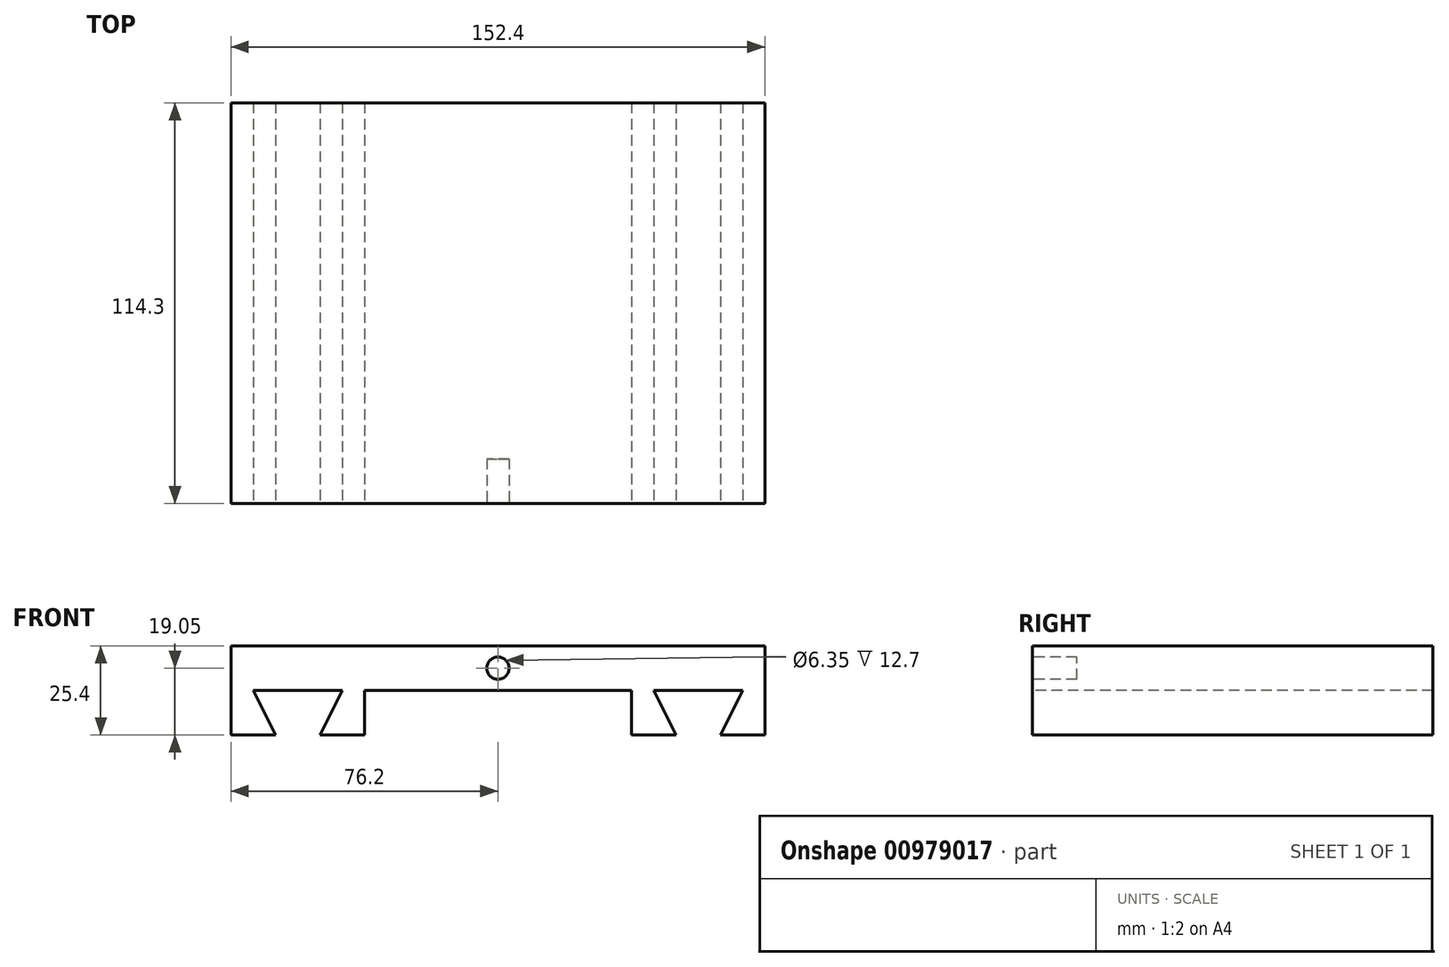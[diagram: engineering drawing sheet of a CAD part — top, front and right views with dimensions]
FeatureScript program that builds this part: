
annotation { "Feature Type Name" : "Feature", "Feature Type Description" : "" }
export const myFeature = defineFeature(function(context is Context, id is Id, definition is map)
    precondition{}
    {
        {
            var Q0;
            Q0=qCreatedBy(makeId("Top.planeOp"),FACE);
            var sketch = newSketch(context, id + "F0", { "sketchPlane" : qUnion([Q0])});
            skLineSegment(sketch, "E0.bottom", {"start": v(-76.2, 57.15) * mm, "end": v(76.2, 57.15) * mm});
            skLineSegment(sketch, "E0.top", {"start": v(-76.2, -57.15) * mm, "end": v(76.2, -57.15) * mm});
            skLineSegment(sketch, "E0.left", {"start": v(-76.2, 57.15) * mm, "end": v(-76.2, -57.15) * mm});
            skLineSegment(sketch, "E0.right", {"start": v(76.2, 57.15) * mm, "end": v(76.2, -57.15) * mm});
            skPoint(sketch, "E0.middle", {"position": v(0, 0) * mm});
            skSolve(sketch);
        }
        {
            var Q0;
            Q0=makeQuery(id+"F0.imprint","IMPRINT",FACE,{"disambiguationData":[TD([[makeQuery(id+"F0.imprint","IMPRINT",EDGE,{"derivedFrom":sQuery(id+"F0.wireOp",EDGE,"E0.bottom")}),-1.0]])]});
            extrude(context, id + "F1", {"entities" : qUnion([Q0]), "depth" : 12.7 * mm, "offsetDistance" : 25.4 * mm});
        }
        {
            var Q0;
            Q0=makeQuery(id+"F1.opExtrude","SWEPT_FACE",FACE,{"disambiguationData":[OSD([sQuery(id+"F0.wireOp",EDGE,"E0.top")])]});
            var sketch = newSketch(context, id + "F2", { "sketchPlane" : qUnion([Q0])});
            skLineSegment(sketch, "E1.bottom", {"start": v(-76.2, 0) * mm, "end": v(-38.1, 0) * mm});
            skLineSegment(sketch, "E1.top", {"start": v(-76.2, -12.7) * mm, "end": v(-38.1, -12.7) * mm});
            skLineSegment(sketch, "E1.left", {"start": v(-76.2, 0) * mm, "end": v(-76.2, -12.7) * mm});
            skLineSegment(sketch, "E1.right", {"start": v(-38.1, 0) * mm, "end": v(-38.1, -12.7) * mm});
            skLineSegment(sketch, "E2.bottom", {"start": v(76.2, 0) * mm, "end": v(38.1, 0) * mm});
            skLineSegment(sketch, "E2.top", {"start": v(76.2, -12.7) * mm, "end": v(38.1, -12.7) * mm});
            skLineSegment(sketch, "E2.left", {"start": v(76.2, 0) * mm, "end": v(76.2, -12.7) * mm});
            skLineSegment(sketch, "E2.right", {"start": v(38.1, 0) * mm, "end": v(38.1, -12.7) * mm});
            skLineSegment(sketch, "E3", {"start": v(-63.5, -12.7) * mm, "end": v(-69.85, 0) * mm});
            skLineSegment(sketch, "E4", {"start": v(-69.85, 0) * mm, "end": v(-69.85, -12.7) * mm});
            skLineSegment(sketch, "E5", {"start": v(-50.8, -12.7) * mm, "end": v(-44.45, 0) * mm});
            skLineSegment(sketch, "E6", {"start": v(-44.45, 0) * mm, "end": v(-44.45, -12.7) * mm});
            skLineSegment(sketch, "E7", {"start": v(50.8, -12.7) * mm, "end": v(44.45, 0) * mm});
            skLineSegment(sketch, "E8", {"start": v(44.45, 0) * mm, "end": v(44.45, -12.7) * mm});
            skLineSegment(sketch, "E9", {"start": v(63.5, -12.7) * mm, "end": v(69.85, 0) * mm});
            skLineSegment(sketch, "E10", {"start": v(69.85, 0) * mm, "end": v(69.85, -12.7) * mm});
            skSolve(sketch);
        }
        {
            var Q0;
            {var subQ0=sQuery(id+"F2.wireOp",EDGE,"E3");Q0=makeQuery(id+"F2.imprint","IMPRINT",FACE,{"disambiguationData":[TD([[makeQuery(id+"F2.imprint","IMPRINT",EDGE,{"derivedFrom":subQ0}),1.0]])]});}
            var Q1;
            {var subQ0=sQuery(id+"F2.wireOp",EDGE,"E1.left");Q1=makeQuery(id+"F2.imprint","IMPRINT",FACE,{"disambiguationData":[TD([[makeQuery(id+"F2.imprint","IMPRINT",EDGE,{"derivedFrom":subQ0}),1.0]])]});}
            var Q2;
            {var subQ0=sQuery(id+"F2.wireOp",EDGE,"E5");Q2=makeQuery(id+"F2.imprint","IMPRINT",FACE,{"disambiguationData":[TD([[makeQuery(id+"F2.imprint","IMPRINT",EDGE,{"derivedFrom":subQ0}),-1.0]])]});}
            var Q3;
            {var subQ0=sQuery(id+"F2.wireOp",EDGE,"E1.right");Q3=makeQuery(id+"F2.imprint","IMPRINT",FACE,{"disambiguationData":[TD([[makeQuery(id+"F2.imprint","IMPRINT",EDGE,{"derivedFrom":subQ0}),-1.0]])]});}
            var Q4;
            {var subQ0=sQuery(id+"F2.wireOp",EDGE,"E2.right");Q4=makeQuery(id+"F2.imprint","IMPRINT",FACE,{"disambiguationData":[TD([[makeQuery(id+"F2.imprint","IMPRINT",EDGE,{"derivedFrom":subQ0}),1.0]])]});}
            var Q5;
            {var subQ0=sQuery(id+"F2.wireOp",EDGE,"E7");Q5=makeQuery(id+"F2.imprint","IMPRINT",FACE,{"disambiguationData":[TD([[makeQuery(id+"F2.imprint","IMPRINT",EDGE,{"derivedFrom":subQ0}),1.0]])]});}
            var Q6;
            {var subQ0=sQuery(id+"F2.wireOp",EDGE,"E9");Q6=makeQuery(id+"F2.imprint","IMPRINT",FACE,{"disambiguationData":[TD([[makeQuery(id+"F2.imprint","IMPRINT",EDGE,{"derivedFrom":subQ0}),-1.0]])]});}
            var Q7;
            {var subQ0=sQuery(id+"F2.wireOp",EDGE,"E2.left");Q7=makeQuery(id+"F2.imprint","IMPRINT",FACE,{"disambiguationData":[TD([[makeQuery(id+"F2.imprint","IMPRINT",EDGE,{"derivedFrom":subQ0}),-1.0]])]});}
            extrude(context, id + "F3", {"entities" : qUnion([Q0, Q1, Q2, Q3, Q4, Q5, Q6, Q7]), "operationType" : NewBodyOperationType.ADD, "oppositeDirection" : true, "depth" : 114.3 * mm, "offsetDistance" : 25.4 * mm});
        }
        {
            var Q0;
            {var subQ0=sQuery(id+"F2.wireOp",EDGE,"E2.top");var subQ1=sQuery(id+"F2.wireOp",EDGE,"E2.bottom");var subQ2=sQuery(id+"F2.wireOp",EDGE,"E1.top");var subQ3=sQuery(id+"F2.wireOp",EDGE,"E1.bottom");Q0=makeQuery(id+"F3.boolean.opBoolean","MERGE",FACE,{"derivedFrom":[makeQuery(id+"F1.opExtrude","SWEPT_FACE",FACE,{"disambiguationData":[OSD([sQuery(id+"F0.wireOp",EDGE,"E0.top")])]}),makeQuery(id+"F3.opExtrude","CAP_FACE",FACE,{"disambiguationData":[OSD([subQ3,subQ2,sQuery(id+"F2.wireOp",EDGE,"E1.left"),sQuery(id+"F2.wireOp",EDGE,"E3")])],"isStart":true}),makeQuery(id+"F3.opExtrude","CAP_FACE",FACE,{"disambiguationData":[OSD([subQ3,subQ2,sQuery(id+"F2.wireOp",EDGE,"E1.right"),sQuery(id+"F2.wireOp",EDGE,"E5")])],"isStart":true}),makeQuery(id+"F3.opExtrude","CAP_FACE",FACE,{"disambiguationData":[OSD([subQ1,subQ0,sQuery(id+"F2.wireOp",EDGE,"E2.right"),sQuery(id+"F2.wireOp",EDGE,"E7")])],"isStart":true}),makeQuery(id+"F3.opExtrude","CAP_FACE",FACE,{"disambiguationData":[OSD([subQ1,subQ0,sQuery(id+"F2.wireOp",EDGE,"E2.left"),sQuery(id+"F2.wireOp",EDGE,"E9")])],"isStart":true})]});}
            var sketch = newSketch(context, id + "F4", { "sketchPlane" : qUnion([Q0])});
            skCircle(sketch, "E11", {"center": v(0, 6.35) * mm, "radius": 3.18 * mm});
            skSolve(sketch);
        }
        {
            var Q0;
            Q0 = qSketchRegion(id + "F4", true);
            extrude(context, id + "F5", {"entities" : qUnion([Q0]), "operationType" : NewBodyOperationType.REMOVE, "oppositeDirection" : true, "depth" : 12.7 * mm, "offsetDistance" : 25.4 * mm});
        }
    });
